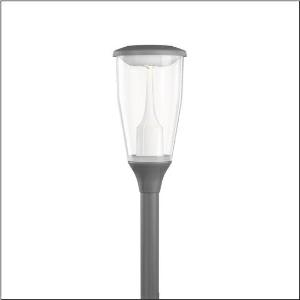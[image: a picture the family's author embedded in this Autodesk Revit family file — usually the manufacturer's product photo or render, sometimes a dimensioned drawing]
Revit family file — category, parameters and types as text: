
# Revit family: dl_11_iq___st1_2a_5xa5565kf14hp00022_5c81
name_source: partatom
category: Lighting Fixtures
units: mm (PartAtom-declared; Revit-internal decimal feet)

## family parameters
Cut with Voids When Loaded = No
Host = Face
Light Source = No
Part Type = Normal
Room Calculation Point = No
Round Connector Dimension = Use Diameter
Shared = No

## types (1)
- --- (1 x LED, 5060 lm, 33.6 W, 4000K)
    Apparent Load = 34 VA
    CIE Flux Codes = 33 63 91 94 100
    Color Rendering = 70
    Color Temperature = 4000K
    Default Elevation = 1800 mm
    Description = DL 11 iQ, mast luminaire, Module 540 iQ-SR, primary light control with 3 zone facetted reflector, of plastic, silver coated, highly specular, structured, primary optical cover: cover, of PMMA, transparent, light distribution: ST1.2a, light emission: direct distribution, primary light characteristic: asymmetric, installation type: post-top, LED, High Power LED, light colour: 740, colour temperature: 4000K, control: Street-Remote, Auto-Match, Temp-Guard, Lumen-Switch, Night-Set, Smart-Wire, Light-Fading, Desk-Remote (wireless, voltage-free reading and setting of iQ features in the workshop via application-optimized NFC function/RFID function), optimised constant luminous flux control (CLO 2.0), mains connection: 220..240V, AC, 50/60Hz, connection cable pre-assembled, cable length: 5,5m, start of lifetime: 34W, end of service life: 36W, luminaire housing, upper part, of diecast aluminium, coated, Siteco® metallic grey (DB 702S), spigot size: 60mm (post-top), post-top mast mounting element, of diecast aluminium, coated, Siteco® metallic grey (DB 702S), Module 540 iQ-SR, traffic white (RAL 9016), equipment: Power, protection rating (complete): IP66, insulation class (complete): insulation class II (safety insulation), certification: CE, ENEC, ENEC+, VDE, packaging unit: 1 piece

Light Distribution: ST1.2a
    Height = 665 mm
    Lamp = 1 x LED
    Lamp Light Flux = 5060 lm
    Lamp Power = 33.6 W
    Lamp count = 1
    Length = 334 mm
    Luminous efficacy = 151 lm/W
    Manufacturer = Siteco
    ModVariant = No
    Model = 5XA5565KF14HP00022
    Number of Poles = 1
    OnlyDefault = Yes
    Power Factor = 1
    Product Name = DL 11 iQ | ST1.2a
    Product group = mast luminaire | pylon top
    ProductGroupID = 6100
    Protection Class = Protection class II
    Protection Degree = IP 66
    RLX_Detail_Level = 1
    RLX_Emergency_Light_Flux = 0 lm
    RLX_Emergency_Type = 0
    RLX_Emergency_Type_DB = No
    RlxData = <blob elided: 160513 chars, md5=6ee5307a>
    Socket = socket
    Standby Power = 0 W
    System Light Flux = 5060 lm
    System Power = 34 W
    Type Comments = factory setting: luminous flux: 100 % | dim-lin: 254 | 695 mA
    Type Image = l_1258354.jpg
    URL = http://relux.com
    VarID = @adj_020035
    Voltage = 0 V
    Weight = 0.00 kg
    Width = 0 mm  [stored 0 ft]

note: [stored X ft] marks values corroborated as IEEE doubles in the binary element streams (Revit-internal decimal feet)

## geometry (parser evidence)
native form markers: Blend x4, Sweep x13
no freeform markers — native parametric forms only
